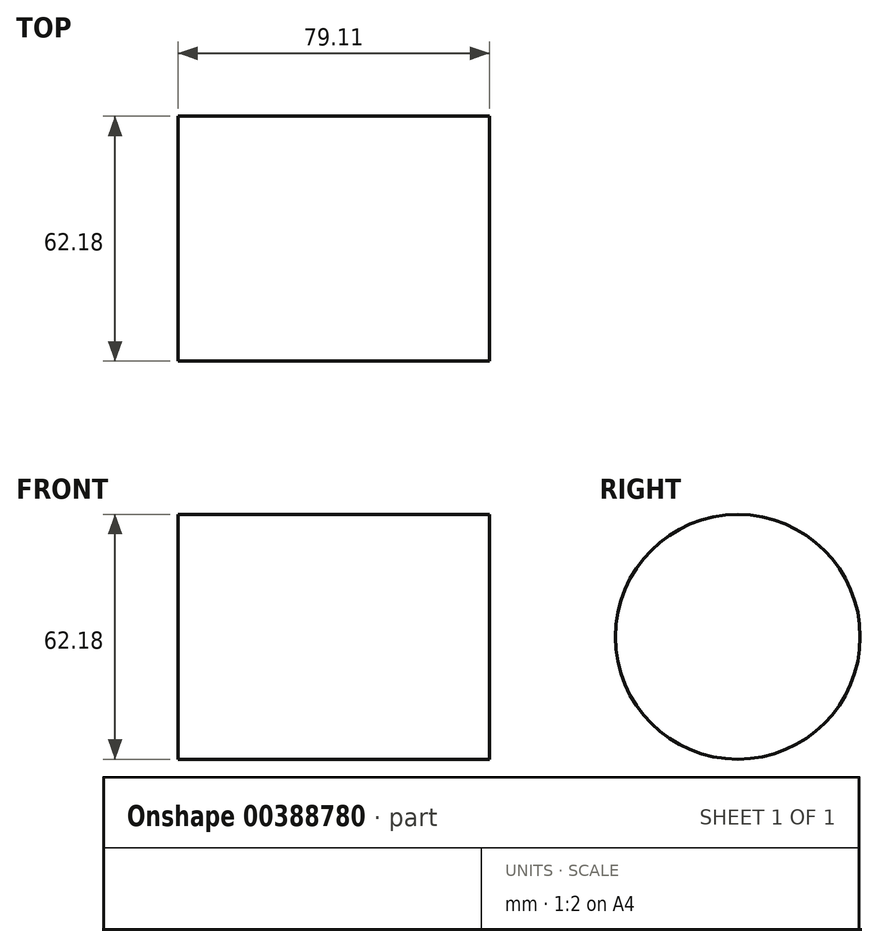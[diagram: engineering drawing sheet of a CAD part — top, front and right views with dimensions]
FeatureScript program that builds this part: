
annotation { "Feature Type Name" : "Feature", "Feature Type Description" : "" }
export const myFeature = defineFeature(function(context is Context, id is Id, definition is map)
    precondition{}
    {
        {
            var Q0;
            Q0=qCreatedBy(makeId("Front.planeOp"),FACE);
            var sketch = newSketch(context, id + "F0", { "sketchPlane" : qUnion([Q0])});
            skLineSegment(sketch, "E0", {"start": v(-64.45, 0) * mm, "end": v(65.64, 0) * mm, "construction": true});
            skLineSegment(sketch, "E1", {"start": v(-39.2, 0) * mm, "end": v(-39.2, 31.1) * mm});
            skLineSegment(sketch, "E2", {"start": v(-39.2, 31.1) * mm, "end": v(39.91, 31.1) * mm});
            skLineSegment(sketch, "E3", {"start": v(39.91, 31.1) * mm, "end": v(39.91, 0) * mm});
            skLineSegment(sketch, "E4", {"start": v(-39.2, 0) * mm, "end": v(39.91, 0) * mm});
            skSolve(sketch);
        }
        {
            var Q0;
            Q0=makeQuery(id+"F0.imprint","IMPRINT",FACE,{"disambiguationData":[TD([[makeQuery(id+"F0.imprint","IMPRINT",EDGE,{"derivedFrom":sQuery(id+"F0.wireOp",EDGE,"E1")}),-1.0]])]});
            var Q1;
            Q1=sQuery(id+"F0.wireOp",EDGE,"E0");
            revolve(context, id + "F1", {"entities" : qUnion([Q0]), "axis" : qUnion([Q1]), "revolveType" : RevolveType.FULL});
        }
    });
